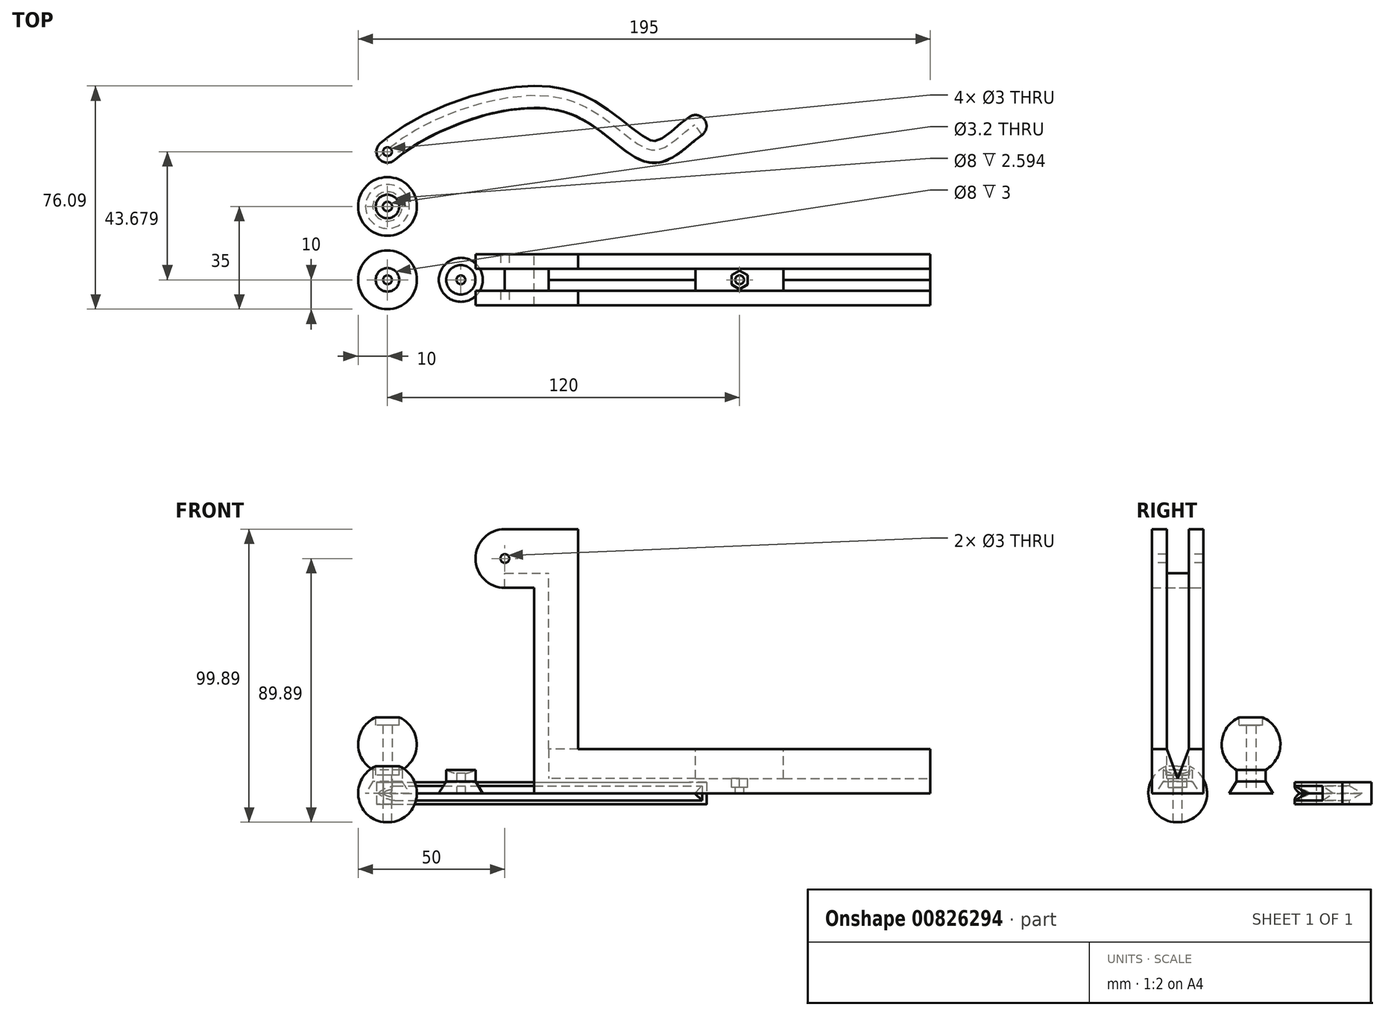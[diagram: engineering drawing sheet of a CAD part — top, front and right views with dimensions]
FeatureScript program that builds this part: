
annotation { "Feature Type Name" : "Feature", "Feature Type Description" : "" }
export const myFeature = defineFeature(function(context is Context, id is Id, definition is map)
    precondition{}
    {
        {
            var Q0;
            Q0=qCreatedBy(makeId("Top.planeOp"),FACE);
            var sketch = newSketch(context, id + "F0", { "sketchPlane" : qUnion([Q0])});
            skArc(sketch, "E0", {"start": v(0, -10) * mm, "mid": v(10, 0) * mm, "end": v(0, 10) * mm});
            skLineSegment(sketch, "E1", {"start": v(0, 10) * mm, "end": v(0, -10) * mm});
            skSolve(sketch);
        }
        {
            var Q0;
            Q0 = qSketchRegion(id + "F0", true);
            var Q1;
            Q1=sQuery(id+"F0.wireOp",EDGE,"E1");
            revolve(context, id + "F1", {"surfaceOperationType" : NewSurfaceOperationType.NEW, "entities" : qUnion([Q0]), "axis" : qUnion([Q1]), "revolveType" : RevolveType.FULL});
        }
        {
            var Q0;
            Q0=qCreatedBy(makeId("Top.planeOp"),FACE);
            cPlane(context, id + "F2", {"entities" : qUnion([Q0]), "cplaneType" : CPlaneType.OFFSET, "offset" : 10 * mm, "width" : 150 * mm, "height" : 150 * mm});
        }
        {
            var Q0;
            Q0=qCreatedBy(id+"F2.planeOp",FACE);
            var sketch = newSketch(context, id + "F3", { "sketchPlane" : qUnion([Q0])});
            skPoint(sketch, "E2", {"position": v(0, 0) * mm});
            skSolve(sketch);
        }
        {
            var Q0;
            Q0=sQuery(id+"F3.wireOp",VERTEX,"E2");
            var Q1;
            Q1=makeQuery(id+"F1.opRevolve","SWEPT_BODY",BODY,{"disambiguationData":[OSD([sQuery(id+"F0.wireOp",EDGE,"E0"),sQuery(id+"F0.wireOp",EDGE,"E1")])]});
            hole(context, id + "F4", {"style" : HoleStyle.C_BORE, "endStyle" : HoleEndStyle.THROUGH, "holeDiameter" : 3 * mm, "cBoreDiameter" : 8 * mm, "cBoreDepth" : 3 * mm, "majorDiameter" : 5 * mm, "isTappedThrough" : true, "tappedDepth" : 12 * mm, "tapClearance" : 3, "locations" : qUnion([Q0]), "scope" : qUnion([Q1])});
        }
        {
            var Q0;
            Q0=qCreatedBy(makeId("Top.planeOp"),FACE);
            var sketch = newSketch(context, id + "F5", { "sketchPlane" : qUnion([Q0])});
            skCircle(sketch, "E3", {"center": v(25, 0) * mm, "radius": 5 * mm});
            skCircle(sketch, "E4", {"center": v(25, 0) * mm, "radius": 1.5 * mm});
            skSolve(sketch);
        }
        {
            var Q0;
            Q0 = qSketchRegion(id + "F5", true);
            extrude(context, id + "F6", {"entities" : qUnion([Q0]), "depth" : 8 * mm, "offsetDistance" : 25 * mm});
        }
        {
            var Q0;
            Q0=qCreatedBy(makeId("Front.planeOp"),FACE);
            var sketch = newSketch(context, id + "F7", { "sketchPlane" : qUnion([Q0])});
            skLineSegment(sketch, "E5", {"start": v(20, 8) * mm, "end": v(25, 0) * mm, "construction": true});
            skLineSegment(sketch, "E6", {"start": v(25, 0) * mm, "end": v(30, 8) * mm, "construction": true});
            skLineSegment(sketch, "E7", {"start": v(25, 26.66) * mm, "end": v(25, 6.66) * mm});
            skArc(sketch, "E8", {"start": v(25, 6.66) * mm, "mid": v(35, 16.66) * mm, "end": v(25, 26.66) * mm});
            skArc(sketch, "E9", {"start": v(25, 26.66) * mm, "mid": v(15, 16.66) * mm, "end": v(25, 6.66) * mm, "construction": true});
            skSolve(sketch);
        }
        {
            var Q0;
            Q0 = qSketchRegion(id + "F7", true);
            var Q1;
            Q1=sQuery(id+"F7.wireOp",EDGE,"E7");
            revolve(context, id + "F8", {"surfaceOperationType" : NewSurfaceOperationType.NEW, "entities" : qUnion([Q0]), "axis" : qUnion([Q1]), "revolveType" : RevolveType.FULL});
        }
        {
            var Q0;
            Q0=makeQuery(id+"F8.opRevolve","SWEPT_BODY",BODY,{"disambiguationData":[OSD([sQuery(id+"F7.wireOp",EDGE,"E7"),sQuery(id+"F7.wireOp",EDGE,"E8")])]});
            var Q1;
            Q1=makeQuery(id+"F6.opExtrude","SWEPT_BODY",BODY,{"disambiguationData":[OSD([sQuery(id+"F5.wireOp",EDGE,"E3"),sQuery(id+"F5.wireOp",EDGE,"E4")])]});
            booleanBodies(context, id + "F9", {"operationType" : BooleanOperationType.SUBTRACTION, "tools" : qUnion([Q0]), "targets" : qUnion([Q1])});
        }
        {
            var Q0;
            Q0=qCreatedBy(makeId("Front.planeOp"),FACE);
            var sketch = newSketch(context, id + "F10", { "sketchPlane" : qUnion([Q0])});
            skLineSegment(sketch, "E10.bottom", {"start": v(50, 0) * mm, "end": v(185, 0) * mm});
            skLineSegment(sketch, "E10.top", {"start": v(50, 90) * mm, "end": v(65, 90) * mm});
            skLineSegment(sketch, "E10.left", {"start": v(50, 0) * mm, "end": v(50, 70) * mm});
            skLineSegment(sketch, "E10.right", {"start": v(185, 0) * mm, "end": v(185, 15) * mm});
            skLineSegment(sketch, "E11.top", {"start": v(185, 15) * mm, "end": v(65, 15) * mm});
            skLineSegment(sketch, "E11.right", {"start": v(65, 90) * mm, "end": v(65, 15) * mm});
            skLineSegment(sketch, "E12", {"start": v(50, 90) * mm, "end": v(40, 90) * mm});
            skLineSegment(sketch, "E13", {"start": v(40, 70) * mm, "end": v(50, 70) * mm});
            skArc(sketch, "E14", {"start": v(40, 90) * mm, "mid": v(30, 80) * mm, "end": v(40, 70) * mm});
            skSolve(sketch);
        }
        {
            var Q0;
            Q0 = qSketchRegion(id + "F10", true);
            extrude(context, id + "F11", {"entities" : qUnion([Q0]), "endBound" : BoundingType.SYMMETRIC, "depth" : (7.5 + 10) * mm, "offsetDistance" : 25 * mm});
        }
        {
            var Q0;
            Q0=makeQuery(id+"F11.opExtrude","SWEPT_FACE",FACE,{"disambiguationData":[OSD([sQuery(id+"F10.wireOp",EDGE,"E10.top")])]});
            var Q1;
            Q1=makeQuery(id+"F11.opExtrude","SWEPT_FACE",FACE,{"disambiguationData":[OSD([sQuery(id+"F10.wireOp",EDGE,"E11.right")])]});
            var Q2;
            Q2=makeQuery(id+"F11.opExtrude","SWEPT_FACE",FACE,{"disambiguationData":[OSD([sQuery(id+"F10.wireOp",EDGE,"E10.right")])]});
            var Q3;
            Q3=makeQuery(id+"F11.opExtrude","SWEPT_FACE",FACE,{"disambiguationData":[OSD([sQuery(id+"F10.wireOp",EDGE,"E11.top")])]});
            var Q4;
            Q4=makeQuery(id+"F11.opExtrude","SWEPT_FACE",FACE,{"disambiguationData":[OSD([sQuery(id+"F10.wireOp",EDGE,"E14")])]});
            shell(context, id + "F12", {"entities" : qUnion([Q0, Q1, Q2, Q3, Q4]), "thickness" : 5 * mm});
        }
        {
            var Q0;
            Q0=makeQuery(id+"F12.opShell","OFFSET_FACE",FACE,{"disambiguationData":[OSD([sQuery(id+"F10.wireOp",EDGE,"E10.bottom")])]});
            var sketch = newSketch(context, id + "F13", { "sketchPlane" : qUnion([Q0])});
            skCircle(sketch, "E15.cCircle", {"center": v(120, 0) * mm, "radius": 2.75 * mm, "construction": true});
            skPoint(sketch, "E15.cCircle.centerSnap0", {"position": v(120, 3.75) * mm});
            skPoint(sketch, "E15.cCircle.centerSnap1", {"position": v(55, 0) * mm});
            skLineSegment(sketch, "E15.0", {"start": v(117.25, -1.59) * mm, "end": v(117.25, 1.59) * mm});
            skLineSegment(sketch, "E15.1", {"start": v(117.25, 1.59) * mm, "end": v(120, 3.18) * mm});
            skLineSegment(sketch, "E15.2", {"start": v(120, 3.18) * mm, "end": v(122.75, 1.59) * mm});
            skLineSegment(sketch, "E15.3", {"start": v(122.75, 1.59) * mm, "end": v(122.75, -1.59) * mm});
            skLineSegment(sketch, "E15.4", {"start": v(122.75, -1.59) * mm, "end": v(120, -3.18) * mm});
            skLineSegment(sketch, "E15.5", {"start": v(120, -3.18) * mm, "end": v(117.25, -1.59) * mm});
            skPoint(sketch, "E15.0.midPoint", {"position": v(117.25, 0) * mm});
            skSolve(sketch);
        }
        {
            var Q0;
            Q0 = qSketchRegion(id + "F13", true);
            extrude(context, id + "F14", {"entities" : qUnion([Q0]), "operationType" : NewBodyOperationType.REMOVE, "oppositeDirection" : true, "depth" : 3 * mm, "offsetDistance" : 25 * mm});
        }
        {
            var Q0;
            Q0=sQuery(id+"F13.wireOp",VERTEX,"E15.cCircle.center");
            var Q1;
            Q1=makeQuery(id+"F11.opExtrude","SWEPT_BODY",BODY,{"disambiguationData":[OSD([sQuery(id+"F10.wireOp",EDGE,"E10.bottom"),sQuery(id+"F10.wireOp",EDGE,"E10.top"),sQuery(id+"F10.wireOp",EDGE,"E10.left"),sQuery(id+"F10.wireOp",EDGE,"E10.right"),sQuery(id+"F10.wireOp",EDGE,"E11.top"),sQuery(id+"F10.wireOp",EDGE,"E11.right")])]});
            hole(context, id + "F15", {"style" : HoleStyle.SIMPLE, "endStyle" : HoleEndStyle.THROUGH, "holeDiameter" : 3 * mm, "majorDiameter" : 5 * mm, "isTappedThrough" : true, "tappedDepth" : 12 * mm, "tapClearance" : 3, "locations" : qUnion([Q0]), "scope" : qUnion([Q1])});
        }
        {
            var Q0;
            Q0=makeQuery(id+"F11.opExtrude","CAP_FACE",FACE,{"disambiguationData":[OSD([sQuery(id+"F10.wireOp",EDGE,"E10.bottom"),sQuery(id+"F10.wireOp",EDGE,"E10.top"),sQuery(id+"F10.wireOp",EDGE,"E10.left"),sQuery(id+"F10.wireOp",EDGE,"E10.right"),sQuery(id+"F10.wireOp",EDGE,"E11.top"),sQuery(id+"F10.wireOp",EDGE,"E11.right"),sQuery(id+"F10.wireOp",EDGE,"E12"),sQuery(id+"F10.wireOp",EDGE,"E13"),sQuery(id+"F10.wireOp",EDGE,"E14")])],"isStart":false});
            var sketch = newSketch(context, id + "F16", { "sketchPlane" : qUnion([Q0])});
            skPoint(sketch, "E16", {"position": v(40, 80) * mm});
            skSolve(sketch);
        }
        {
            var Q0;
            Q0=sQuery(id+"F16.wireOp",VERTEX,"E16");
            var Q1;
            Q1=makeQuery(id+"F11.opExtrude","SWEPT_BODY",BODY,{"disambiguationData":[OSD([sQuery(id+"F10.wireOp",EDGE,"E10.bottom"),sQuery(id+"F10.wireOp",EDGE,"E10.top"),sQuery(id+"F10.wireOp",EDGE,"E10.left"),sQuery(id+"F10.wireOp",EDGE,"E10.right"),sQuery(id+"F10.wireOp",EDGE,"E11.top"),sQuery(id+"F10.wireOp",EDGE,"E11.right"),sQuery(id+"F10.wireOp",EDGE,"E12"),sQuery(id+"F10.wireOp",EDGE,"E13"),sQuery(id+"F10.wireOp",EDGE,"E14")])]});
            hole(context, id + "F17", {"style" : HoleStyle.SIMPLE, "endStyle" : HoleEndStyle.THROUGH, "holeDiameter" : 3 * mm, "majorDiameter" : 5 * mm, "isTappedThrough" : true, "tappedDepth" : 12 * mm, "tapClearance" : 3, "locations" : qUnion([Q0]), "scope" : qUnion([Q1])});
        }
        {
            var Q0;
            Q0=qCreatedBy(makeId("Top.planeOp"),FACE);
            var sketch = newSketch(context, id + "F18", { "sketchPlane" : qUnion([Q0])});
            skCircle(sketch, "E17", {"center": v(0, 43.68) * mm, "radius": 1.5 * mm});
            skFitSpline(sketch, "E18", {"points": [v(0, 43.68) * mm, v(60, 61.18) * mm, v(90, 43.68) * mm, v(105, 52.43) * mm], "startDerivative": vector(79.56, 69.42) * mm, "endDerivative": vector(72.1, 52.12) * mm, "construction": true});
            skLineSegment(sketch, "E19", {"start": v(90, 43.68) * mm, "end": v(0, 43.68) * mm, "construction": true});
            skArc(sketch, "E20.0.startCap", {"start": v(2.47, 40.85) * mm, "mid": v(-2.83, 41.21) * mm, "end": v(-2.47, 46.5) * mm});
            skArc(sketch, "E20.0.endCap", {"start": v(102.8, 55.47) * mm, "mid": v(108.04, 54.63) * mm, "end": v(107.2, 49.39) * mm});
            skFitSpline(sketch, "E20.0.left", {"points": [v(-2.47, 46.5) * mm, v(-1.55, 47.3) * mm, v(0.44, 48.9) * mm, v(5, 52.03) * mm, v(11.68, 55.82) * mm, v(20.86, 59.91) * mm, v(30.77, 63.25) * mm, v(39.27, 65.12) * mm, v(46.03, 65.9) * mm, v(51.02, 66.09) * mm, v(55.07, 65.85) * mm, v(58.23, 65.4) * mm, v(60.17, 65.01) * mm, v(61.69, 64.62) * mm, v(63.17, 64.18) * mm, v(64.96, 63.56) * mm, v(67.02, 62.7) * mm, v(69.65, 61.44) * mm, v(72.7, 59.67) * mm, v(76.04, 57.4) * mm, v(79.08, 55.1) * mm, v(81.84, 52.89) * mm, v(84.34, 50.9) * mm, v(86.57, 49.24) * mm, v(88.16, 48.26) * mm, v(89.22, 47.75) * mm, v(89.79, 47.55) * mm, v(90.17, 47.45) * mm, v(90.42, 47.4) * mm, v(90.63, 47.38) * mm, v(90.93, 47.37) * mm, v(91.3, 47.4) * mm, v(91.98, 47.54) * mm, v(93.03, 47.96) * mm, v(94.58, 48.91) * mm, v(96.34, 50.25) * mm, v(98.29, 51.87) * mm, v(100.42, 53.66) * mm, v(101.98, 54.87) * mm, v(102.8, 55.47) * mm]});
            skFitSpline(sketch, "E20.0.right", {"points": [v(2.47, 40.85) * mm, v(3.2, 41.5) * mm, v(4.89, 42.84) * mm, v(8.92, 45.62) * mm, v(15.05, 49.1) * mm, v(23.6, 52.92) * mm, v(32.8, 56.01) * mm, v(40.59, 57.72) * mm, v(46.61, 58.42) * mm, v(50.96, 58.58) * mm, v(54.38, 58.38) * mm, v(56.96, 58.01) * mm, v(58.5, 57.7) * mm, v(59.69, 57.39) * mm, v(60.86, 57.04) * mm, v(62.28, 56.55) * mm, v(63.95, 55.86) * mm, v(66.1, 54.82) * mm, v(68.7, 53.33) * mm, v(71.64, 51.32) * mm, v(74.45, 49.2) * mm, v(77.13, 47.05) * mm, v(79.72, 44.98) * mm, v(82.27, 43.09) * mm, v(84.44, 41.73) * mm, v(86.27, 40.85) * mm, v(87.47, 40.4) * mm, v(88.48, 40.14) * mm, v(89.27, 39.98) * mm, v(90.07, 39.9) * mm, v(91.13, 39.85) * mm, v(92.42, 39.96) * mm, v(94.38, 40.39) * mm, v(96.58, 41.32) * mm, v(98.91, 42.78) * mm, v(101.06, 44.43) * mm, v(103.13, 46.15) * mm, v(105.16, 47.85) * mm, v(106.52, 48.9) * mm, v(107.2, 49.39) * mm]});
            skLineSegment(sketch, "E21", {"start": v(60, 61.18) * mm, "end": v(60, 43.68) * mm, "construction": true});
            skLineSegment(sketch, "E22", {"start": v(60, 52.43) * mm, "end": v(105, 52.43) * mm, "construction": true});
            skLineSegment(sketch, "E23", {"start": v(2.47, 40.85) * mm, "end": v(-7.26, 32.37) * mm});
            skSolve(sketch);
        }
        {
            var Q0;
            Q0=makeQuery(id+"F18.imprint","IMPRINT",FACE,{"disambiguationData":[TD([[makeQuery(id+"F18.imprint","IMPRINT",EDGE,{"derivedFrom":sQuery(id+"F18.wireOp",EDGE,"E17")}),-1.0]])]});
            extrude(context, id + "F19", {"entities" : qUnion([Q0]), "endBound" : BoundingType.SYMMETRIC, "depth" : 7.5 * mm, "offsetDistance" : 25 * mm});
        }
        {
            var Q0;
            Q0=sQuery(id+"F18.wireOp",EDGE,"E23");
            var Q1;
            Q1=sQuery(id+"F18.wireOp",VERTEX,"E23.end");
            cPlane(context, id + "F20", {"entities" : qUnion([Q0, Q1]), "cplaneType" : CPlaneType.LINE_POINT, "offset" : 25 * mm, "width" : 150 * mm, "height" : 150 * mm});
        }
        {
            var Q0;
            Q0=qCreatedBy(id+"F20.planeOp",FACE);
            var sketch = newSketch(context, id + "F21", { "sketchPlane" : qUnion([Q0])});
            skLineSegment(sketch, "E24", {"start": v(-29.16, 2.5) * mm, "end": v(-29.16, -2.5) * mm});
            skLineSegment(sketch, "E25", {"start": v(-29.16, -2.5) * mm, "end": v(-33.5, 0) * mm});
            skLineSegment(sketch, "E26", {"start": v(-33.5, 0) * mm, "end": v(-29.16, 2.5) * mm});
            skSolve(sketch);
        }
        {
            var Q0;
            Q0=makeQuery(id+"F21.imprint","IMPRINT",FACE,{"disambiguationData":[TD([[makeQuery(id+"F21.imprint","IMPRINT",EDGE,{"derivedFrom":sQuery(id+"F21.wireOp",EDGE,"E24")}),-1.0]])]});
            var Q1;
            Q1=sQuery(id+"F18.wireOp",EDGE,"E23");
            var Q2;
            Q2=sQuery(id+"F18.wireOp",EDGE,"E20.0.right");
            sweep(context, id + "F22", {"operationType" : NewBodyOperationType.REMOVE, "profiles" : qUnion([Q0]), "path" : qUnion([Q1, Q2])});
        }
        {
            var Q0;
            Q0=makeQuery(id+"F12.opShell","OFFSET_FACE",FACE,{"disambiguationData":[OSD([sQuery(id+"F10.wireOp",EDGE,"E10.left")])]});
            var sketch = newSketch(context, id + "F23", { "sketchPlane" : qUnion([Q0])});
            skLineSegment(sketch, "E27", {"start": v(-3.75, 15) * mm, "end": v(0, 5) * mm});
            skLineSegment(sketch, "E28", {"start": v(0, 5) * mm, "end": v(3.75, 15) * mm});
            skLineSegment(sketch, "E29.top", {"start": v(-3.75, 5) * mm, "end": v(3.75, 5) * mm});
            skLineSegment(sketch, "E29.left", {"start": v(-3.75, 15) * mm, "end": v(-3.75, 5) * mm});
            skLineSegment(sketch, "E29.right", {"start": v(3.75, 15) * mm, "end": v(3.75, 5) * mm});
            skSolve(sketch);
        }
        {
            var Q0;
            Q0 = qSketchRegion(id + "F23", true);
            extrude(context, id + "F24", {"entities" : qUnion([Q0]), "operationType" : NewBodyOperationType.ADD, "depth" : 50 * mm, "offsetDistance" : 25 * mm});
        }
        {
            var Q0;
            Q0=makeQuery(id+"F11.opExtrude","SWEPT_FACE",FACE,{"disambiguationData":[OSD([sQuery(id+"F10.wireOp",EDGE,"E10.right")])]});
            var sketch = newSketch(context, id + "F25", { "sketchPlane" : qUnion([Q0])});
            skLineSegment(sketch, "E30", {"start": v(-3.75, 15) * mm, "end": v(0, 5) * mm});
            skLineSegment(sketch, "E31", {"start": v(0, 5) * mm, "end": v(3.75, 15) * mm});
            skLineSegment(sketch, "E32.top", {"start": v(-3.75, 5) * mm, "end": v(3.75, 5) * mm});
            skLineSegment(sketch, "E32.left", {"start": v(-3.75, 15) * mm, "end": v(-3.75, 5) * mm});
            skLineSegment(sketch, "E32.right", {"start": v(3.75, 16.78) * mm, "end": v(3.75, 5) * mm});
            skSolve(sketch);
        }
        {
            var Q0;
            Q0 = qSketchRegion(id + "F25", true);
            extrude(context, id + "F26", {"entities" : qUnion([Q0]), "operationType" : NewBodyOperationType.ADD, "oppositeDirection" : true, "depth" : 50 * mm, "offsetDistance" : 25 * mm});
        }
        {
            var Q0;
            Q0=makeQuery(id+"F6.opExtrude","CAP_FACE",FACE,{"disambiguationData":[OSD([sQuery(id+"F5.wireOp",EDGE,"E3"),sQuery(id+"F5.wireOp",EDGE,"E4")])],"isStart":true});
            var sketch = newSketch(context, id + "F27", { "sketchPlane" : qUnion([Q0])});
            skCircle(sketch, "E33", {"center": v(25, 0) * mm, "radius": 7.5 * mm});
            skCircle(sketch, "E34", {"center": v(25, 0) * mm, "radius": 1.5 * mm});
            skSolve(sketch);
        }
        {
            var Q0;
            Q0 = qSketchRegion(id + "F27", true);
            extrude(context, id + "F28", {"entities" : qUnion([Q0]), "operationType" : NewBodyOperationType.ADD, "oppositeDirection" : true, "depth" : 4 * mm, "offsetDistance" : 25 * mm});
        }
        {
            var Q0;
            Q0=makeQuery(id+"F28.opExtrude","CAP_EDGE",EDGE,{"disambiguationData":[OSD([sQuery(id+"F27.wireOp",EDGE,"E33")])],"isStart":false});
            chamfer(context, id + "F29", {"entities" : qUnion([Q0]), "chamferType" : ChamferType.TWO_OFFSETS, "width1" : 4 * mm, "oppositeDirection" : false, "width2" : 2.5 * mm, "tangentPropagation" : true});
        }
        {
            var Q0;
            Q0=qCreatedBy(makeId("Top.planeOp"),FACE);
            var sketch = newSketch(context, id + "F30", { "sketchPlane" : qUnion([Q0])});
            skCircle(sketch, "E35", {"center": v(0, 25) * mm, "radius": 7.5 * mm});
            skCircle(sketch, "E36", {"center": v(0, 25) * mm, "radius": 1.6 * mm});
            skSolve(sketch);
        }
        {
            var Q0;
            Q0 = qSketchRegion(id + "F30", true);
            extrude(context, id + "F31", {"entities" : qUnion([Q0]), "depth" : 4 * mm, "offsetDistance" : 25 * mm});
        }
        {
            var Q0;
            Q0=makeQuery(id+"F31.opExtrude","CAP_FACE",FACE,{"disambiguationData":[OSD([sQuery(id+"F30.wireOp",EDGE,"E35"),sQuery(id+"F30.wireOp",EDGE,"E36")])],"isStart":false});
            var sketch = newSketch(context, id + "F32", { "sketchPlane" : qUnion([Q0])});
            skCircle(sketch, "E37", {"center": v(0, 25) * mm, "radius": 5 * mm});
            skCircle(sketch, "E38", {"center": v(0, 25) * mm, "radius": 1.6 * mm});
            skSolve(sketch);
        }
        {
            var Q0;
            Q0 = qSketchRegion(id + "F32", true);
            extrude(context, id + "F33", {"entities" : qUnion([Q0]), "operationType" : NewBodyOperationType.ADD, "depth" : 4 * mm, "offsetDistance" : 25 * mm});
        }
        {
            var Q0;
            Q0=qCreatedBy(makeId("Front.planeOp"),FACE);
            var Q1;
            Q1=sQuery(id+"F32.wireOp",VERTEX,"E37.center");
            cPlane(context, id + "F34", {"entities" : qUnion([Q0, Q1]), "cplaneType" : CPlaneType.PLANE_POINT, "offset" : 25 * mm, "width" : 150 * mm, "height" : 150 * mm});
        }
        {
            var Q0;
            Q0=qCreatedBy(id+"F34.planeOp",FACE);
            var sketch = newSketch(context, id + "F35", { "sketchPlane" : qUnion([Q0])});
            skArc(sketch, "E39", {"start": v(1.6, 6.79) * mm, "mid": v(10, 16.66) * mm, "end": v(1.6, 26.53) * mm});
            skLineSegment(sketch, "E40", {"start": v(1.6, 6.79) * mm, "end": v(1.6, 26.53) * mm});
            skLineSegment(sketch, "E41", {"start": v(0, 8) * mm, "end": v(5, 8) * mm, "construction": true});
            skLineSegment(sketch, "E42", {"start": v(0, 8) * mm, "end": v(0, 16.66) * mm, "construction": true});
            skSolve(sketch);
        }
        {
            var Q0;
            Q0=makeQuery(id+"F35.imprint","IMPRINT",FACE,{"disambiguationData":[TD([[makeQuery(id+"F35.imprint","IMPRINT",EDGE,{"derivedFrom":sQuery(id+"F35.wireOp",EDGE,"E39")}),1.0]])]});
            var Q1;
            Q1=sQuery(id+"F35.wireOp",EDGE,"E42");
            revolve(context, id + "F36", {"operationType" : NewBodyOperationType.ADD, "surfaceOperationType" : NewSurfaceOperationType.NEW, "entities" : qUnion([Q0]), "axis" : qUnion([Q1]), "revolveType" : RevolveType.FULL});
        }
        {
            var Q0;
            Q0=makeQuery(id+"F31.opExtrude","CAP_EDGE",EDGE,{"disambiguationData":[OSD([sQuery(id+"F30.wireOp",EDGE,"E35")])],"isStart":false});
            chamfer(context, id + "F37", {"entities" : qUnion([Q0]), "chamferType" : ChamferType.TWO_OFFSETS, "width1" : 2.5 * mm, "oppositeDirection" : false, "width2" : 4 * mm, "tangentPropagation" : true});
        }
        {
            var Q0;
            Q0=sQuery(id+"F35.wireOp",VERTEX,"E39.end");
            var Q1;
            Q1=qCreatedBy(makeId("Top.planeOp"),FACE);
            cPlane(context, id + "F38", {"entities" : qUnion([Q0, Q1]), "cplaneType" : CPlaneType.PLANE_POINT, "offset" : 25 * mm, "width" : 150 * mm, "height" : 150 * mm});
        }
        {
            var Q0;
            Q0=qCreatedBy(id+"F38.planeOp",FACE);
            var sketch = newSketch(context, id + "F39", { "sketchPlane" : qUnion([Q0])});
            skCircle(sketch, "E43", {"center": v(0, 25) * mm, "radius": 4 * mm});
            skSolve(sketch);
        }
        {
            var Q0;
            Q0 = qSketchRegion(id + "F39", true);
            extrude(context, id + "F40", {"entities" : qUnion([Q0]), "operationType" : NewBodyOperationType.REMOVE, "oppositeDirection" : true, "depth" : 3.3 * mm, "offsetDistance" : 25 * mm});
        }
    });
